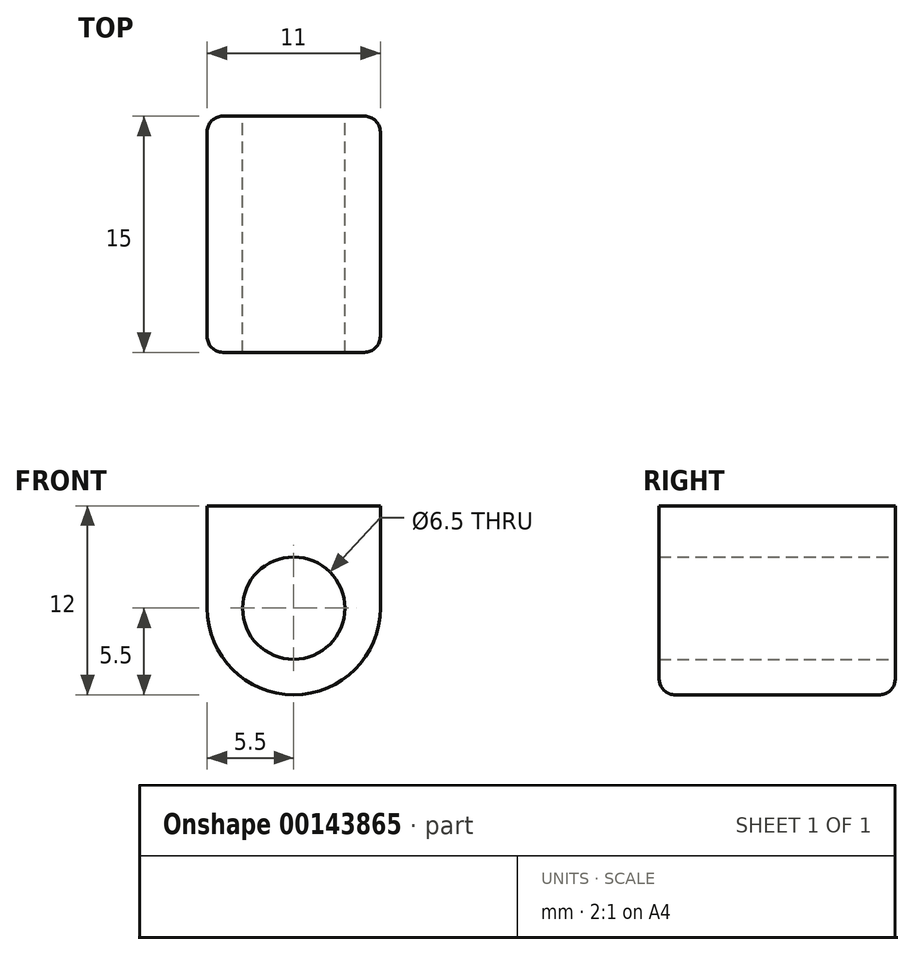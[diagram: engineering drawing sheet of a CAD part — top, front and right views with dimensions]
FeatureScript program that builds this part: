
annotation { "Feature Type Name" : "Feature", "Feature Type Description" : "" }
export const myFeature = defineFeature(function(context is Context, id is Id, definition is map)
    precondition{}
    {
        {
            var Q0;
            Q0=qCreatedBy(makeId("Front.planeOp"),FACE);
            var sketch = newSketch(context, id + "F0", { "sketchPlane" : qUnion([Q0])});
            skCircle(sketch, "E0", {"center": v(0, 0) * mm, "radius": 5.5 * mm});
            skCircle(sketch, "E1", {"center": v(0, 0) * mm, "radius": 3.25 * mm});
            skLineSegment(sketch, "E2", {"start": v(-5.5, 0) * mm, "end": v(-5.5, 6.5) * mm});
            skLineSegment(sketch, "E3", {"start": v(5.5, 0) * mm, "end": v(5.5, 6.5) * mm});
            skLineSegment(sketch, "E4", {"start": v(5.5, 6.5) * mm, "end": v(-5.5, 6.5) * mm});
            skSolve(sketch);
        }
        {
            var Q0;
            Q0=makeQuery(id+"F0.imprint","IMPRINT",FACE,{"disambiguationData":[TD([[makeQuery(id+"F0.imprint","IMPRINT",EDGE,{"derivedFrom":sQuery(id+"F0.wireOp",EDGE,"E1")}),-1.0]])]});
            var Q1;
            {var subQ0=sQuery(id+"F0.wireOp",EDGE,"E2");Q1=makeQuery(id+"F0.imprint","IMPRINT",FACE,{"disambiguationData":[TD([[makeQuery(id+"F0.imprint","IMPRINT",EDGE,{"derivedFrom":subQ0}),-1.0]])]});}
            extrude(context, id + "F1", {"entities" : qUnion([Q0, Q1]), "depth" : 15 * mm, "offsetDistance" : 25 * mm});
        }
        {
            var Q0;
            Q0=makeQuery(id+"F1.opExtrude","CAP_EDGE",EDGE,{"disambiguationData":[OSD([sQuery(id+"F0.wireOp",EDGE,"E0")])],"isStart":false});
            var Q1;
            Q1=makeQuery(id+"F1.opExtrude","CAP_EDGE",EDGE,{"disambiguationData":[OSD([sQuery(id+"F0.wireOp",EDGE,"E0")])],"isStart":true});
            fillet(context, id + "F2", {"entities" : qUnion([Q0, Q1]), "radius" : 1 * mm, "tangentPropagation" : true, "allowEdgeOverflow" : false});
        }
    });
